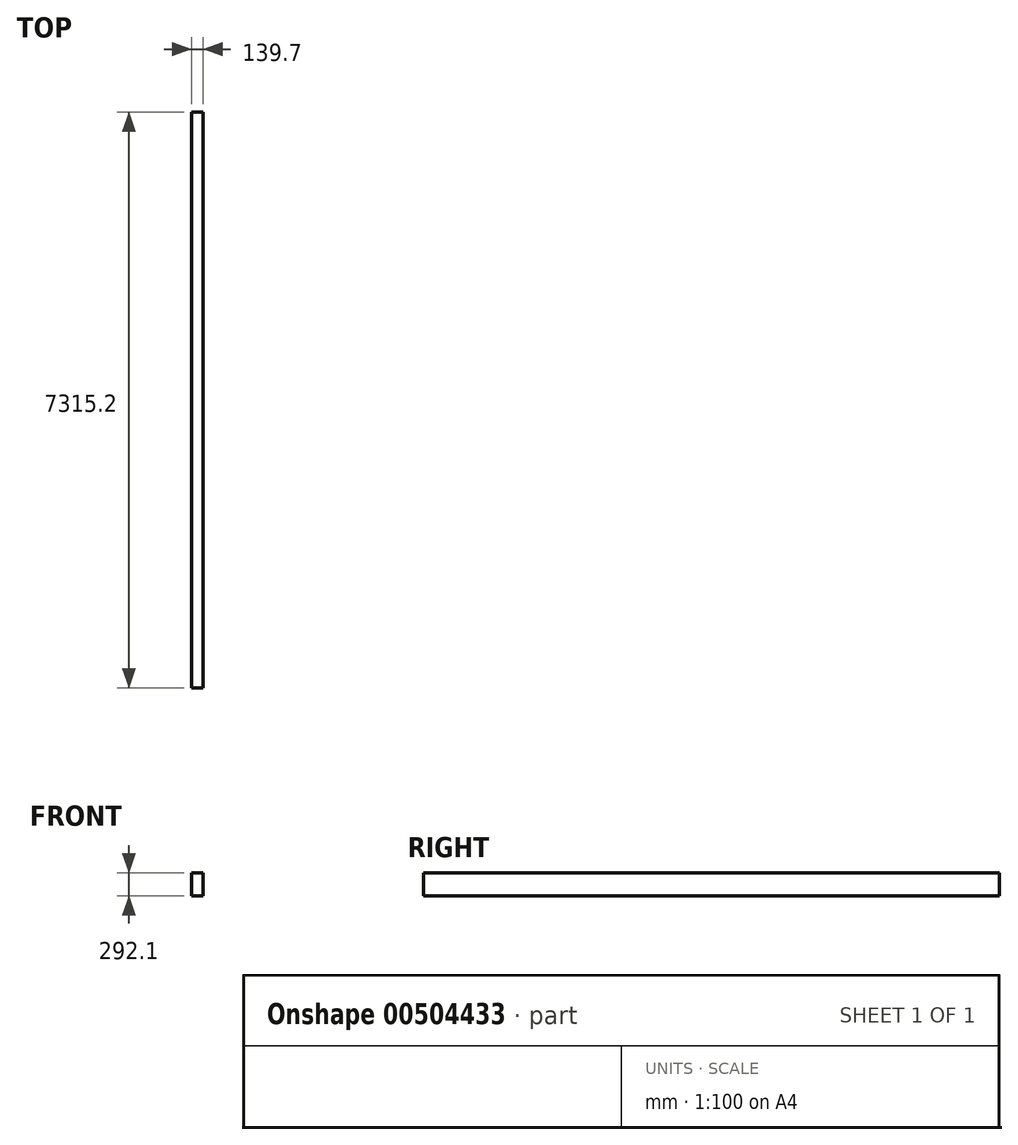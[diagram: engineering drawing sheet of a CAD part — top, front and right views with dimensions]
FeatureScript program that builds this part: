
annotation { "Feature Type Name" : "Feature", "Feature Type Description" : "" }
export const myFeature = defineFeature(function(context is Context, id is Id, definition is map)
    precondition{}
    {
        {
            var Q0;
            Q0=qCreatedBy(makeId("Front.planeOp"),FACE);
            var sketch = newSketch(context, id + "F0", { "sketchPlane" : qUnion([Q0])});
            skLineSegment(sketch, "E0.bottom", {"start": v(0, 0) * mm, "end": v(139.7, 0) * mm});
            skLineSegment(sketch, "E0.top", {"start": v(0, 292.1) * mm, "end": v(139.7, 292.1) * mm});
            skLineSegment(sketch, "E0.left", {"start": v(0, 0) * mm, "end": v(0, 292.1) * mm});
            skLineSegment(sketch, "E0.right", {"start": v(139.7, 0) * mm, "end": v(139.7, 292.1) * mm});
            skSolve(sketch);
        }
        {
            var Q0;
            Q0 = qSketchRegion(id + "F0", true);
            extrude(context, id + "F1", {"entities" : qUnion([Q0]), "depth" : 7315.2 * mm});
        }
    });
